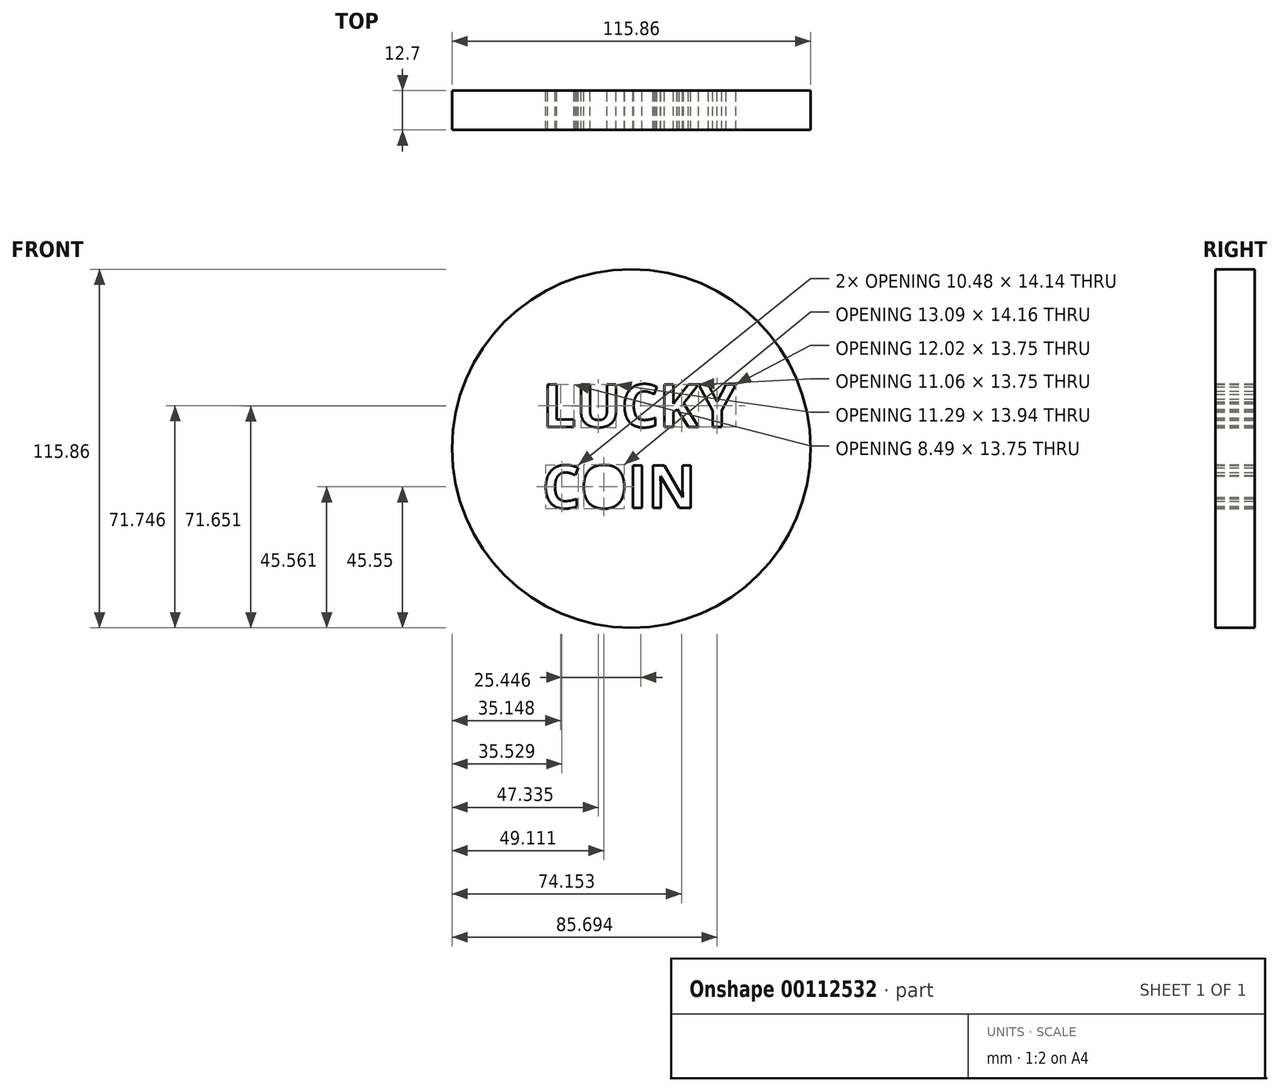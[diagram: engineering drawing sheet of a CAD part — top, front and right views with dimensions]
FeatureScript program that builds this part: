
annotation { "Feature Type Name" : "Feature", "Feature Type Description" : "" }
export const myFeature = defineFeature(function(context is Context, id is Id, definition is map)
    precondition{}
    {
        {
            var Q0;
            Q0=qCreatedBy(makeId("Front.planeOp"),FACE);
            var sketch = newSketch(context, id + "F0", { "sketchPlane" : qUnion([Q0])});
            skCircle(sketch, "E0", {"center": v(0, 0) * mm, "radius": 57.93 * mm});
            skText(sketch, "E1", { "text": "LUCKY\nCOIN", "fontName": "OpenSans-Bold.ttf"});
            const initialGuessF0  = {"E1": [-0.02876, 0.00694, 1, 0, 0.01387]};
            skSetInitialGuess(sketch, initialGuessF0);
            skSolve(sketch);
        }
        {
            var Q0;
            Q0=makeQuery(id+"F0.imprint","IMPRINT",FACE,{"disambiguationData":[TD([[makeQuery(id+"F0.imprint","IMPRINT",EDGE,{"derivedFrom":sQuery(id+"F0.wireOp",EDGE,"E0")}),1.0]])]});
            extrude(context, id + "F1", {"entities" : qUnion([Q0]), "depth" : 12.7 * mm});
        }
    });
